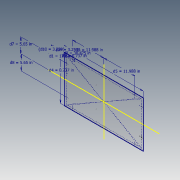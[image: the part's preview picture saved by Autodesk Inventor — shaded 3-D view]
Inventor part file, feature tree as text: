
AUTODESK INVENTOR PART (.ipt)
format: ipt  version: 2020.3 (Build 243373000, 373)  size: 124,928 bytes
history: native  units: in
note: dims shown in document units (in); Inventor stores cm internally (conversion verified against a paired STEP export)
features: sketch x2, hole x2, extrude x1, fillet x1
ambient origin geometry x8: Origin, YZ Plane, XZ Plane, XY Plane, X Axis, Y Axis, Z Axis, Center Point
bodies: Solid1 (feature_tree)
feature tree (6):
  sketch  "Sketch1"  dims[d0=30.475in d1=17.8in]
  extrude  "Extrusion1"  Depth=17.8in
  hole  "Hole1"  [1 undecoded]
  fillet  "Fillet1"  Radius=11.988in
  hole  "Hole2"  [1 undecoded]
  sketch  "Sketch2"  dims[d3=0.737in d4=0.737in d5=11.988in d6=11.988in d7=5.65in d8=5.65in d9=3.2495in d10=3.25in d11=0.177in d12=0.0in d13=0.3125in d14=0.75in d15=0.375in d16=0.25in d17=0.5635in d18=1.0in d19=0.8108in d20=0.25in d21=3.0in d22=4.0in d24=0.0in d25=4.0in d26=0.123in d27=0.75in d28=0.433in d29=0.236in d30=90.0deg d31=1.0in d32=0.8108in]
note: 2 required parameter values undecoded (feature->parameter linkage not recoverable at this tier; creation-order binding heuristic only, values carry confidence <= 0.55)
